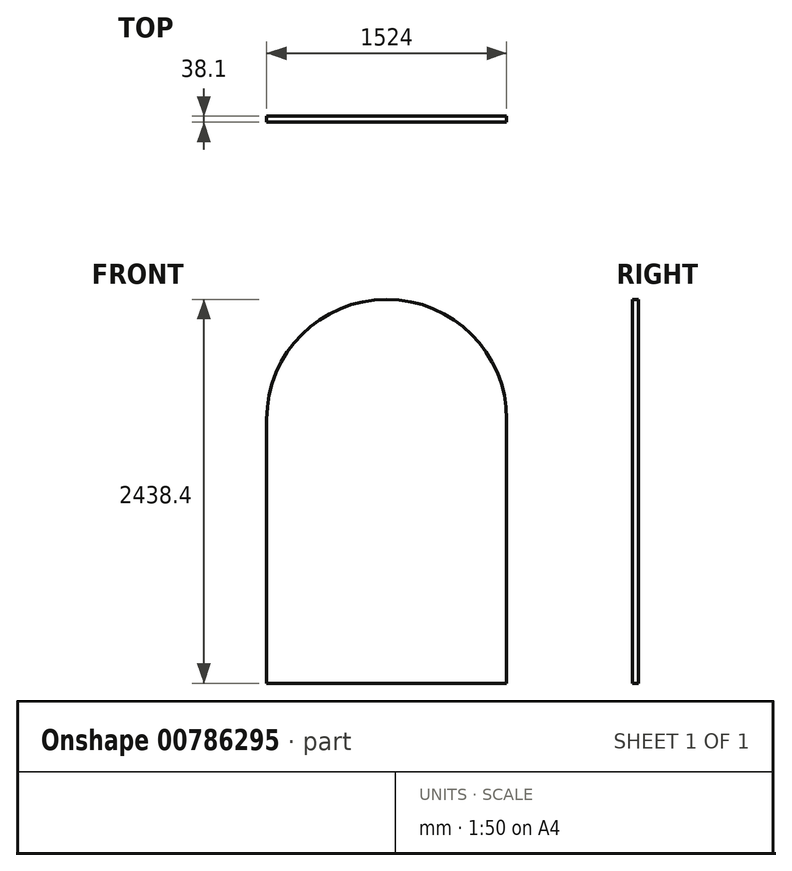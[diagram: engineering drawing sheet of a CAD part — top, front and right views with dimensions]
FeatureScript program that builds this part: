
annotation { "Feature Type Name" : "Feature", "Feature Type Description" : "" }
export const myFeature = defineFeature(function(context is Context, id is Id, definition is map)
    precondition{}
    {
        {
            var Q0;
            Q0=qCreatedBy(makeId("Front.planeOp"),FACE);
            var sketch = newSketch(context, id + "F0", { "sketchPlane" : qUnion([Q0])});
            skArc(sketch, "E0", {"start": v(-762, 0) * mm, "mid": v(0, 762) * mm, "end": v(762, 0) * mm});
            skLineSegment(sketch, "E1.bottom", {"start": v(-914.4, 914.4) * mm, "end": v(914.4, 914.4) * mm});
            skLineSegment(sketch, "E1.top", {"start": v(-914.4, -1676.4) * mm, "end": v(914.4, -1676.4) * mm});
            skLineSegment(sketch, "E1.left", {"start": v(-914.4, 914.4) * mm, "end": v(-914.4, -1676.4) * mm});
            skLineSegment(sketch, "E1.right", {"start": v(914.4, 914.4) * mm, "end": v(914.4, -1676.4) * mm});
            skLineSegment(sketch, "E2", {"start": v(-762, 0) * mm, "end": v(-762, -1676.4) * mm});
            skLineSegment(sketch, "E3", {"start": v(762, 0) * mm, "end": v(762, -1676.4) * mm});
            skLineSegment(sketch, "E4.0", {"start": v(914.4, 0) * mm, "end": v(914.4, -1676.4) * mm});
            skArc(sketch, "E4.1", {"start": v(-914.4, 0) * mm, "mid": v(0, 914.4) * mm, "end": v(914.4, 0) * mm});
            skLineSegment(sketch, "E4.2", {"start": v(-914.4, 0) * mm, "end": v(-914.4, -1676.4) * mm});
            skSolve(sketch);
        }
        {
            var Q0;
            Q0=makeQuery(id+"F0.imprint","IMPRINT",FACE,{"disambiguationData":[TD([[makeQuery(id+"F0.imprint","IMPRINT",EDGE,{"derivedFrom":sQuery(id+"F0.wireOp",EDGE,"E0")}),1.0]])]});
            extrude(context, id + "F1", {"entities" : qUnion([Q0]), "depth" : 38.1 * mm, "offsetDistance" : 25.4 * mm});
        }
    });
